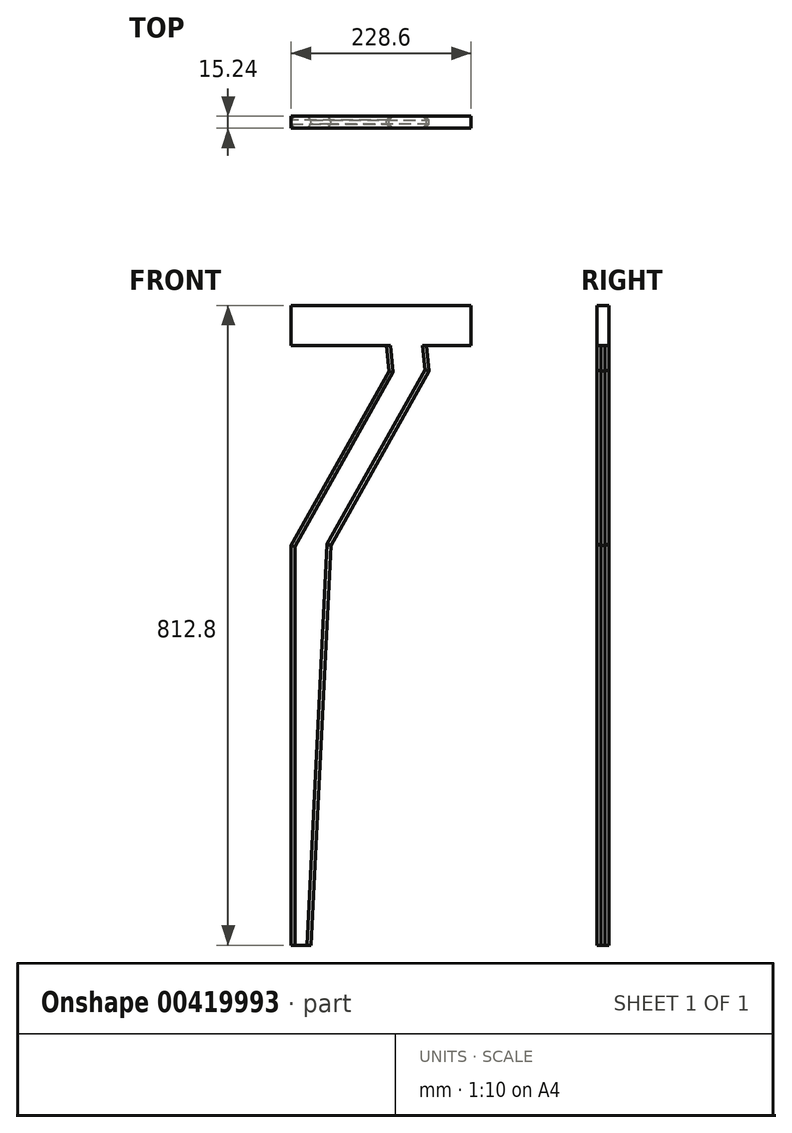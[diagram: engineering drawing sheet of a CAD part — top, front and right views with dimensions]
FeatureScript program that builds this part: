
annotation { "Feature Type Name" : "Feature", "Feature Type Description" : "" }
export const myFeature = defineFeature(function(context is Context, id is Id, definition is map)
    precondition{}
    {
        {
            var Q0;
            Q0=qCreatedBy(makeId("Front.planeOp"),FACE);
            var sketch = newSketch(context, id + "F0", { "sketchPlane" : qUnion([Q0])});
            skLineSegment(sketch, "E0", {"start": v(0, 0) * mm, "end": v(25.4, 0) * mm});
            skLineSegment(sketch, "E1", {"start": v(50.8, 508) * mm, "end": v(175.28, 729.4) * mm});
            skLineSegment(sketch, "E2", {"start": v(175.28, 729.4) * mm, "end": v(172.05, 762) * mm});
            skLineSegment(sketch, "E3", {"start": v(172.05, 762) * mm, "end": v(228.6, 762) * mm});
            skLineSegment(sketch, "E4", {"start": v(228.6, 762) * mm, "end": v(228.6, 812.8) * mm});
            skLineSegment(sketch, "E5", {"start": v(228.6, 812.8) * mm, "end": v(0, 812.8) * mm});
            skLineSegment(sketch, "E6", {"start": v(0, 812.8) * mm, "end": v(0, 762) * mm});
            skLineSegment(sketch, "E7", {"start": v(0, 762) * mm, "end": v(121, 762) * mm});
            skLineSegment(sketch, "E8", {"start": v(121, 762) * mm, "end": v(124.27, 729.03) * mm});
            skLineSegment(sketch, "E9", {"start": v(124.27, 729.03) * mm, "end": v(0, 508) * mm});
            skLineSegment(sketch, "E10", {"start": v(0, 508) * mm, "end": v(0, 0) * mm});
            skLineSegment(sketch, "E11", {"start": v(50.8, 508) * mm, "end": v(25.4, 0) * mm});
            skPoint(sketch, "E12.orphan", {"position": v(50.8, 0) * mm});
            skSolve(sketch);
        }
        {
            var Q0;
            Q0=makeQuery(id+"F0.imprint","IMPRINT",FACE,{"disambiguationData":[TD([[makeQuery(id+"F0.imprint","IMPRINT",EDGE,{"derivedFrom":sQuery(id+"F0.wireOp",EDGE,"E0")}),1.0]])]});
            extrude(context, id + "F1", {"entities" : qUnion([Q0]), "depth" : 15.24 * mm});
        }
        {
            var Q0;
            Q0=makeQuery(id+"F1.opExtrude","CAP_EDGE",EDGE,{"disambiguationData":[OSD([sQuery(id+"F0.wireOp",EDGE,"E1")])],"isStart":false});
            var Q1;
            Q1=makeQuery(id+"F1.opExtrude","CAP_EDGE",EDGE,{"disambiguationData":[OSD([sQuery(id+"F0.wireOp",EDGE,"E11")])],"isStart":false});
            var Q2;
            Q2=makeQuery(id+"F1.opExtrude","CAP_EDGE",EDGE,{"disambiguationData":[OSD([sQuery(id+"F0.wireOp",EDGE,"E10")])],"isStart":false});
            var Q3;
            Q3=makeQuery(id+"F1.opExtrude","CAP_EDGE",EDGE,{"disambiguationData":[OSD([sQuery(id+"F0.wireOp",EDGE,"E9")])],"isStart":false});
            var Q4;
            Q4=makeQuery(id+"F1.opExtrude","CAP_EDGE",EDGE,{"disambiguationData":[OSD([sQuery(id+"F0.wireOp",EDGE,"E10")])],"isStart":true});
            var Q5;
            Q5=makeQuery(id+"F1.opExtrude","CAP_EDGE",EDGE,{"disambiguationData":[OSD([sQuery(id+"F0.wireOp",EDGE,"E9")])],"isStart":true});
            var Q6;
            Q6=makeQuery(id+"F1.opExtrude","CAP_EDGE",EDGE,{"disambiguationData":[OSD([sQuery(id+"F0.wireOp",EDGE,"E11")])],"isStart":true});
            var Q7;
            Q7=makeQuery(id+"F1.opExtrude","CAP_EDGE",EDGE,{"disambiguationData":[OSD([sQuery(id+"F0.wireOp",EDGE,"E1")])],"isStart":true});
            var Q8;
            Q8=makeQuery(id+"F1.opExtrude","CAP_EDGE",EDGE,{"disambiguationData":[OSD([sQuery(id+"F0.wireOp",EDGE,"E8")])],"isStart":true});
            var Q9;
            Q9=makeQuery(id+"F1.opExtrude","CAP_EDGE",EDGE,{"disambiguationData":[OSD([sQuery(id+"F0.wireOp",EDGE,"E2")])],"isStart":true});
            var Q10;
            Q10=makeQuery(id+"F1.opExtrude","CAP_EDGE",EDGE,{"disambiguationData":[OSD([sQuery(id+"F0.wireOp",EDGE,"E2")])],"isStart":false});
            var Q11;
            Q11=makeQuery(id+"F1.opExtrude","CAP_EDGE",EDGE,{"disambiguationData":[OSD([sQuery(id+"F0.wireOp",EDGE,"E8")])],"isStart":false});
            chamfer(context, id + "F2", {"entities" : qUnion([Q0, Q1, Q2, Q3, Q4, Q5, Q6, Q7, Q8, Q9, Q10, Q11]), "width" : 5.08 * mm, "tangentPropagation" : true});
        }
    });
